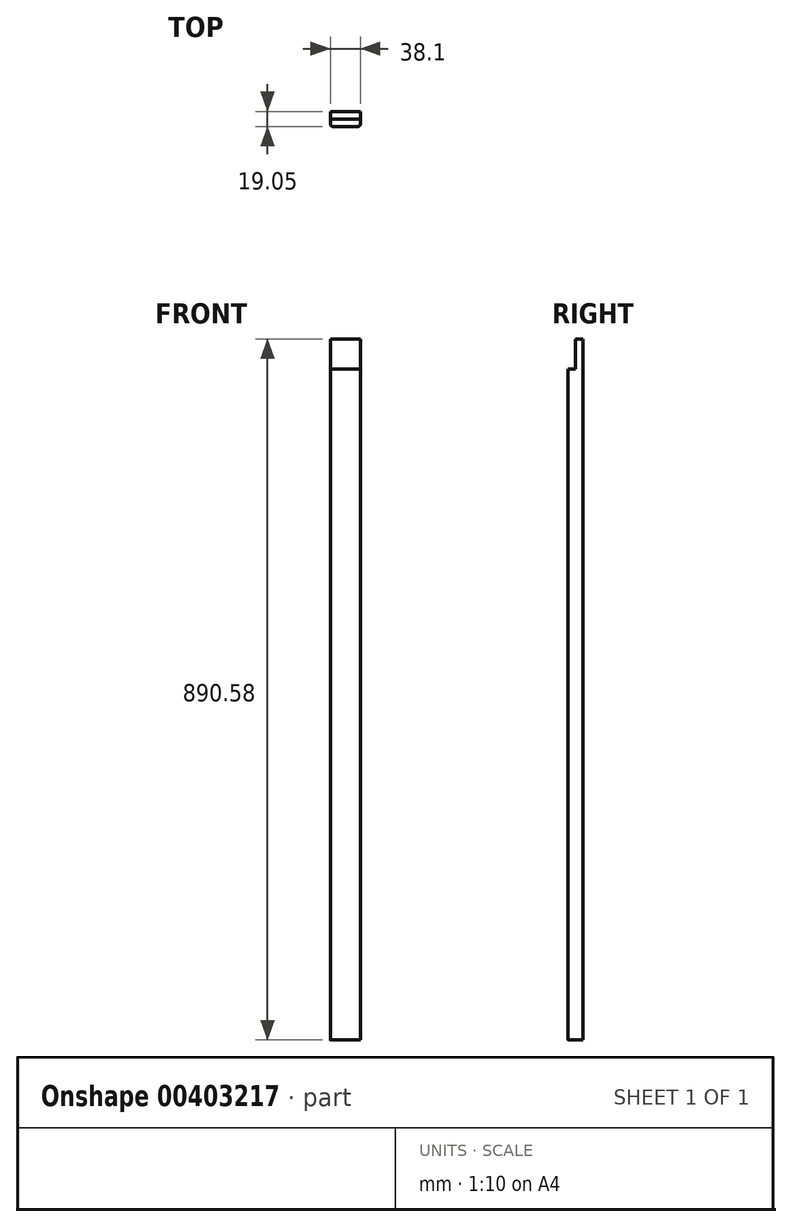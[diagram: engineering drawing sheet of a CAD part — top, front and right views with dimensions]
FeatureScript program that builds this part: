
annotation { "Feature Type Name" : "Feature", "Feature Type Description" : "" }
export const myFeature = defineFeature(function(context is Context, id is Id, definition is map)
    precondition{}
    {
        {
            var Q0;
            Q0=qCreatedBy(makeId("Front.planeOp"),FACE);
            var sketch = newSketch(context, id + "F0", { "sketchPlane" : qUnion([Q0])});
            skLineSegment(sketch, "E0.bottom", {"start": v(19.05, 445.3) * mm, "end": v(-19.05, 445.3) * mm});
            skLineSegment(sketch, "E0.top", {"start": v(19.05, -445.3) * mm, "end": v(-19.05, -445.3) * mm});
            skLineSegment(sketch, "E0.left", {"start": v(19.05, 445.3) * mm, "end": v(19.05, -445.3) * mm});
            skLineSegment(sketch, "E0.right", {"start": v(-19.05, 445.3) * mm, "end": v(-19.05, -445.3) * mm});
            skPoint(sketch, "E0.middle", {"position": v(0, 0) * mm});
            skSolve(sketch);
        }
        {
            var Q0;
            Q0=qSketchRegion(id+"F0",true);
            extrude(context, id + "F1", {"entities" : qUnion([Q0]), "depth" : 19.05 * mm});
        }
        {
            var Q0;
            Q0=makeQuery(id+"F1.opExtrude","CAP_FACE",FACE,{"disambiguationData":[OSD([sQuery(id+"F0.wireOp",EDGE,"E0.bottom"),sQuery(id+"F0.wireOp",EDGE,"E0.top"),sQuery(id+"F0.wireOp",EDGE,"E0.left"),sQuery(id+"F0.wireOp",EDGE,"E0.right")])],"isStart":false});
            var sketch = newSketch(context, id + "F2", { "sketchPlane" : qUnion([Q0])});
            skLineSegment(sketch, "E1.bottom", {"start": v(-19.05, 445.3) * mm, "end": v(19.05, 445.3) * mm});
            skLineSegment(sketch, "E1.top", {"start": v(-19.05, 407.2) * mm, "end": v(19.05, 407.2) * mm});
            skLineSegment(sketch, "E1.left", {"start": v(-19.05, 445.3) * mm, "end": v(-19.05, 407.2) * mm});
            skLineSegment(sketch, "E1.right", {"start": v(19.05, 445.3) * mm, "end": v(19.05, 407.2) * mm});
            skSolve(sketch);
        }
        {
            var Q0;
            Q0 = qSketchRegion(id + "F2", true);
            extrude(context, id + "F3", {"entities" : qUnion([Q0]), "operationType" : NewBodyOperationType.REMOVE, "oppositeDirection" : true, "depth" : 9.52 * mm});
        }
        {
            var Q0;
            Q0=makeQuery(id+"F1.opExtrude","CAP_EDGE",EDGE,{"disambiguationData":[OSD([sQuery(id+"F0.wireOp",EDGE,"E0.right")])],"isStart":false});
            var Q1;
            Q1=makeQuery(id+"F1.opExtrude","CAP_EDGE",EDGE,{"disambiguationData":[OSD([sQuery(id+"F0.wireOp",EDGE,"E0.left")])],"isStart":false});
            fillet(context, id + "F4", {"entities" : qUnion([Q0, Q1]), "radius" : 3.17 * mm, "tangentPropagation" : true, "allowEdgeOverflow" : false});
        }
    });
